# Revit family: Batidora_B-50_GENERADO
name_source: partatom
category: Equipos especializados
units: mm (PartAtom-declared; Revit-internal decimal feet)

## family parameters
Compartido = No
Corte con vacíos al cargar = No
Cota de conector redondo = Diámetro de uso
Número OmniClass = 23.21.21.31.11
Punto de cálculo de habitación = No
Se basa en plano de trabajo = No
Siempre vertical = Sí
Tipo de pieza = Normal

## types (6) — shared parameters
Cycle = 50 Hz
Fabricante = SAMMIC S.L.
Foodservice Equipment Identifier = Sí
Phase = 1
Revision Code = 1
URL = https://www.sammic.com
URL Cutsheet = http://www.sammic.com
zero-valued in all types: Elevación por defecto

## per-type parameters (varying)
| type | Comentarios de tipo | Conn Plug | FL Amps | HP | Modelo | Specification by Manufacturer | Volts | Watts | Weight in Pounds |
| Immersion blender & whisk combo MB-51 230/50-60/1 | Professional hand blender and beater. 570 W. | EU (SCHUKO 2P) | 3 A | 0.76 | 3030691 | · Variable speed motor block.
· 425 mm detachable mixer arm designed for continuous use in recipients of up to 80 l.
· Whisk with capacity for 2 to 80 egg whites. | 230 V | 570 W | 12.5 |
| Immersion blender & whisk combo MB-51 230/50-60/1 AUS | Professional hand blender and beater. 570 W. | AU/NZ (AS 3112 10A / 2P) | 3 A | 0.76 | 3030828 | · Variable speed motor block.
· 425 mm detachable mixer arm designed for continuous use in recipients of up to 80 l.
· Whisk with capacity for 2 to 80 egg whites. | 230 V | 570 W | 10.3 |
| Immersion blender & whisk combo MB-51 120/50-60/1 USA | Professional hand blender and beater. 720 W. | USA (NEMA 5-15P / 2P+G) | 4 A | 0.97 | 3030831 | · Variable speed motor block.
· 425 mm detachable mixer arm designed for continuous use in recipients of up to 80 l.
· Whisk with capacity for 2 to 80 egg whites. | 120 V | 720 W | 10.3 |
| Whisk B-50 230/50-60/1 | Professional beater. 570 W. | EU (SCHUKO 2P) | 3 A | 0.76 | 3030693 | · Variable speed motor block.
· Whisk with capacity for 2 to 80 egg whites. | 230 V | 570 W | 9.7 |
| Whisk B-50 230/50-60/1 AUS | Professional beater. 570 W. |  | 3 A | 0.76 | 3030834 | · Variable speed motor block.
· Whisk with capacity for 2 to 80 egg whites. | 230 V | 570 W | 9.7 |
| Whisk B-50 120/50-60/1 USA | Professional beater. 720 W. | USA (NEMA 5-15P / 2P+G) | 4 A | 0.97 | 3030837 | · Variable speed motor block.
· Whisk with capacity for 2 to 80 egg whites. | 120 V | 720 W | 9.7 |

note: column(s) folded — value = type name in every type: Descripción
